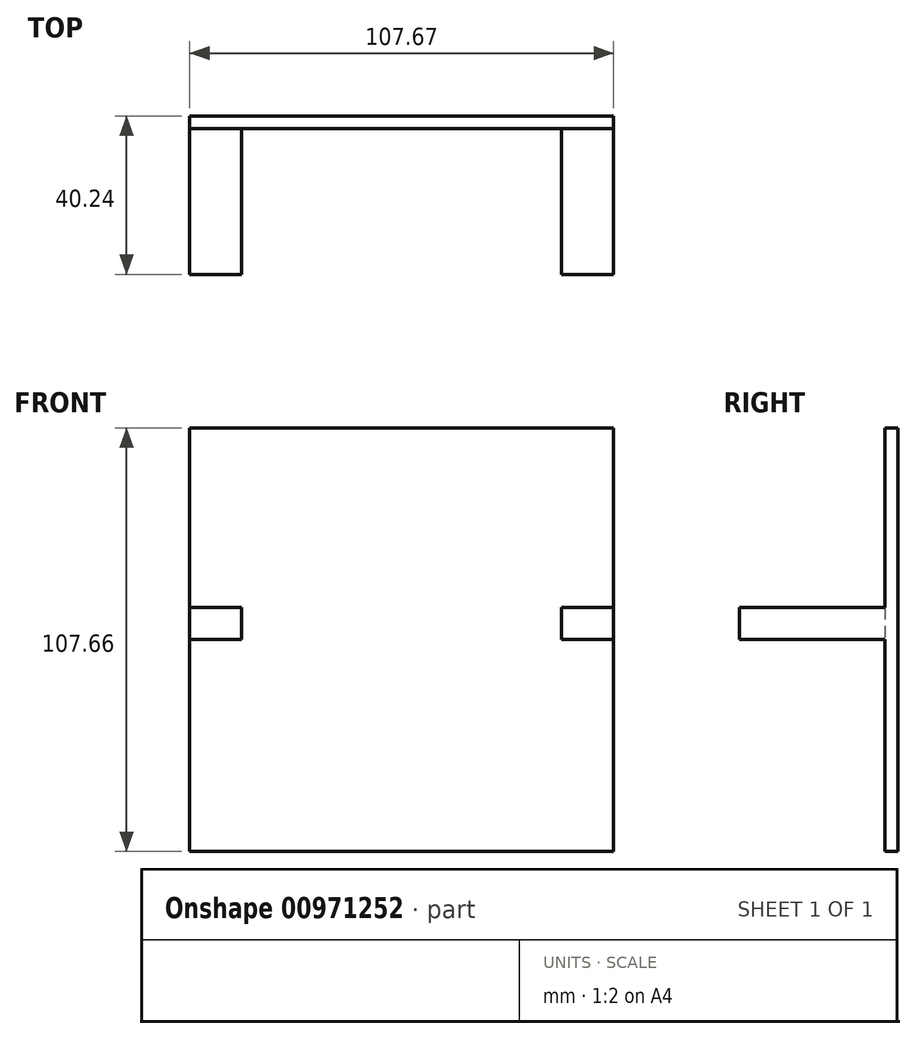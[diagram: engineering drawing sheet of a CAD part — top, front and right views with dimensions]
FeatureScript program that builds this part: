
annotation { "Feature Type Name" : "Feature", "Feature Type Description" : "" }
export const myFeature = defineFeature(function(context is Context, id is Id, definition is map)
    precondition{}
    {
        {
            var Q0;
            Q0=qCreatedBy(makeId("Front.planeOp"),FACE);
            var sketch = newSketch(context, id + "F0", { "sketchPlane" : qUnion([Q0])});
            skLineSegment(sketch, "E0", {"start": v(-94.47, 89.42) * mm, "end": v(-94.47, -18.24) * mm});
            skLineSegment(sketch, "E1", {"start": v(-94.47, -18.24) * mm, "end": v(13.2, -18.24) * mm});
            skLineSegment(sketch, "E2", {"start": v(13.2, -18.24) * mm, "end": v(13.2, 89.42) * mm});
            skLineSegment(sketch, "E3", {"start": v(13.2, 89.42) * mm, "end": v(-94.47, 89.42) * mm});
            skSolve(sketch);
        }
        {
            var Q0;
            Q0=makeQuery(id+"F0.imprint","IMPRINT",FACE,{"disambiguationData":[TD([[makeQuery(id+"F0.imprint","IMPRINT",EDGE,{"derivedFrom":sQuery(id+"F0.wireOp",EDGE,"E0")}),1.0]])]});
            extrude(context, id + "F1", {"entities" : qUnion([Q0]), "depth" : 3.24 * mm, "offsetDistance" : 25.4 * mm});
        }
        {
            var Q0;
            Q0=makeQuery(id+"F1.opExtrude","CAP_FACE",FACE,{"disambiguationData":[OSD([sQuery(id+"F0.wireOp",EDGE,"E0"),sQuery(id+"F0.wireOp",EDGE,"E1"),sQuery(id+"F0.wireOp",EDGE,"E2"),sQuery(id+"F0.wireOp",EDGE,"E3")])],"isStart":false});
            var sketch = newSketch(context, id + "F2", { "sketchPlane" : qUnion([Q0])});
            skLineSegment(sketch, "E4.bottom", {"start": v(0, 43.74) * mm, "end": v(13.2, 43.74) * mm});
            skLineSegment(sketch, "E4.top", {"start": v(0, 35.6) * mm, "end": v(13.2, 35.6) * mm});
            skLineSegment(sketch, "E4.left", {"start": v(0, 43.74) * mm, "end": v(0, 35.6) * mm});
            skLineSegment(sketch, "E4.right", {"start": v(13.2, 43.74) * mm, "end": v(13.2, 35.6) * mm});
            skLineSegment(sketch, "E5", {"start": v(-40.64, 89.42) * mm, "end": v(-40.64, -32.44) * mm});
            skLineSegment(sketch, "E6.MirrorCS", {"start": v(-81.27, 43.74) * mm, "end": v(-94.47, 43.74) * mm});
            skLineSegment(sketch, "E7.MirrorCS", {"start": v(-81.27, 35.6) * mm, "end": v(-94.47, 35.6) * mm});
            skLineSegment(sketch, "E8.MirrorCS", {"start": v(-94.47, 43.74) * mm, "end": v(-94.47, 35.6) * mm});
            skLineSegment(sketch, "E9.MirrorCS", {"start": v(-81.27, 43.74) * mm, "end": v(-81.27, 35.6) * mm});
            skSolve(sketch);
        }
        {
            var Q0;
            Q0=makeQuery(id+"F2.imprint","IMPRINT",FACE,{"disambiguationData":[TD([[makeQuery(id+"F2.imprint","IMPRINT",EDGE,{"derivedFrom":sQuery(id+"F2.wireOp",EDGE,"E6.MirrorCS")}),1.0]])]});
            var Q1;
            Q1=makeQuery(id+"F2.imprint","IMPRINT",FACE,{"disambiguationData":[TD([[makeQuery(id+"F2.imprint","IMPRINT",EDGE,{"derivedFrom":sQuery(id+"F2.wireOp",EDGE,"E4.bottom")}),-1.0]])]});
            extrude(context, id + "F3", {"entities" : qUnion([Q0, Q1]), "operationType" : NewBodyOperationType.ADD, "depth" : 37 * mm, "offsetDistance" : 25.4 * mm});
        }
    });
